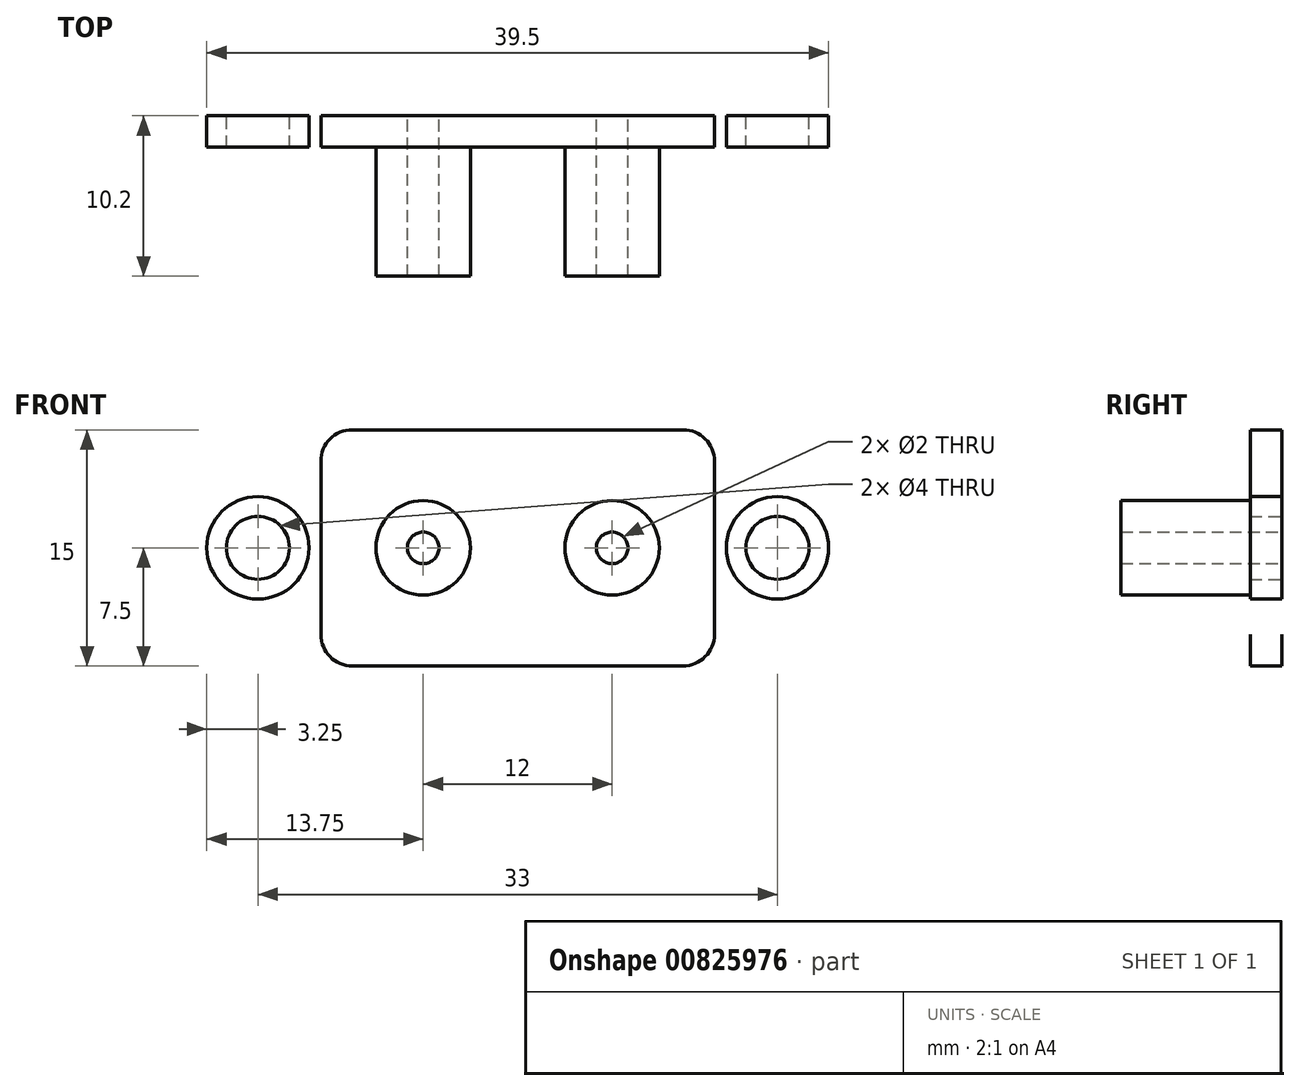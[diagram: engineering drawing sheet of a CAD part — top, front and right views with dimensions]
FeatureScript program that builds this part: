
annotation { "Feature Type Name" : "Feature", "Feature Type Description" : "" }
export const myFeature = defineFeature(function(context is Context, id is Id, definition is map)
    precondition{}
    {
        {
            var Q0;
            Q0=qCreatedBy(makeId("Front.planeOp"),FACE);
            var sketch = newSketch(context, id + "F0", { "sketchPlane" : qUnion([Q0])});
            skPoint(sketch, "E0.middle", {"position": v(0, 0) * mm});
            skLineSegment(sketch, "E1.bottom", {"start": v(10.5, -7.5) * mm, "end": v(-10.5, -7.5) * mm});
            skLineSegment(sketch, "E1.top", {"start": v(10.5, 7.5) * mm, "end": v(-10.5, 7.5) * mm});
            skLineSegment(sketch, "E1.left", {"start": v(12.5, -5.5) * mm, "end": v(12.5, 5.5) * mm});
            skLineSegment(sketch, "E1.right", {"start": v(-12.5, -5.5) * mm, "end": v(-12.5, 5.5) * mm});
            skPoint(sketch, "E2.visualSharp", {"position": v(-12.5, -7.5) * mm});
            skArc(sketch, "E2.filletArc", {"start": v(-12.5, -5.5) * mm, "mid": v(-11.91, -6.91) * mm, "end": v(-10.5, -7.5) * mm});
            skPoint(sketch, "E3.visualSharp", {"position": v(-12.5, 7.5) * mm});
            skArc(sketch, "E3.filletArc", {"start": v(-10.5, 7.5) * mm, "mid": v(-11.91, 6.91) * mm, "end": v(-12.5, 5.5) * mm});
            skPoint(sketch, "E4.visualSharp", {"position": v(12.5, -7.5) * mm});
            skArc(sketch, "E4.filletArc", {"start": v(10.5, -7.5) * mm, "mid": v(11.91, -6.91) * mm, "end": v(12.5, -5.5) * mm});
            skPoint(sketch, "E5.visualSharp", {"position": v(12.5, 7.5) * mm});
            skArc(sketch, "E5.filletArc", {"start": v(12.5, 5.5) * mm, "mid": v(11.91, 6.91) * mm, "end": v(10.5, 7.5) * mm});
            skCircle(sketch, "E6", {"center": v(-6, 0) * mm, "radius": 1 * mm});
            skCircle(sketch, "E7", {"center": v(6, 0) * mm, "radius": 1 * mm});
            skLineSegment(sketch, "E8.bottom", {"start": v(-12.5, 2) * mm, "end": v(-14.2, 2) * mm});
            skLineSegment(sketch, "E8.top", {"start": v(-12.5, -2) * mm, "end": v(-14.2, -2) * mm});
            skLineSegment(sketch, "E8.left", {"start": v(-12.5, 2) * mm, "end": v(-12.5, -2) * mm});
            skLineSegment(sketch, "E8.right", {"start": v(-14.2, 2) * mm, "end": v(-14.2, -2) * mm});
            skPoint(sketch, "E8.middle", {"position": v(-13.35, 0) * mm});
            skPoint(sketch, "E8.middle.positionSnap0", {"position": v(-12.5, 0) * mm});
            skPoint(sketch, "E8.centerSnap0", {"position": v(-12.5, 0) * mm});
            skLineSegment(sketch, "E9.bottom", {"start": v(12.5, 2) * mm, "end": v(14.2, 2) * mm});
            skLineSegment(sketch, "E9.top", {"start": v(12.5, -2) * mm, "end": v(14.2, -2) * mm});
            skLineSegment(sketch, "E9.left", {"start": v(12.5, 2) * mm, "end": v(12.5, -2) * mm});
            skLineSegment(sketch, "E9.right", {"start": v(14.2, 2) * mm, "end": v(14.2, -2) * mm});
            skPoint(sketch, "E9.middle", {"position": v(13.35, 0) * mm});
            skCircle(sketch, "E10", {"center": v(-16.5, 0) * mm, "radius": 3.25 * mm});
            skCircle(sketch, "E11", {"center": v(-16.5, 0) * mm, "radius": 2 * mm});
            skCircle(sketch, "E12", {"center": v(16.5, 0) * mm, "radius": 3.25 * mm});
            skCircle(sketch, "E13", {"center": v(16.5, 0) * mm, "radius": 2 * mm});
            skCircle(sketch, "E14", {"center": v(-6, 0) * mm, "radius": 3 * mm});
            skCircle(sketch, "E15", {"center": v(6, 0) * mm, "radius": 3 * mm});
            skSolve(sketch);
        }
        {
            var Q0;
            Q0=makeQuery(id+"F0.imprint","IMPRINT",FACE,{"disambiguationData":[TD([[makeQuery(id+"F0.imprint","IMPRINT",EDGE,{"derivedFrom":sQuery(id+"F0.wireOp",EDGE,"E1.bottom")}),-1.0]])]});
            var Q1;
            {var subQ0=sQuery(id+"F0.wireOp",EDGE,"E8.left");Q1=makeQuery(id+"F0.imprint","IMPRINT",FACE,{"disambiguationData":[TD([[makeQuery(id+"F0.imprint","IMPRINT",EDGE,{"derivedFrom":subQ0}),-1.0]])]});}
            var Q2;
            {var subQ0=sQuery(id+"F0.wireOp",EDGE,"E8.right");Q2=makeQuery(id+"F0.imprint","IMPRINT",FACE,{"disambiguationData":[TD([[makeQuery(id+"F0.imprint","IMPRINT",EDGE,{"derivedFrom":subQ0}),1.0]])]});}
            var Q3;
            {var subQ5=sQuery(id+"F0.wireOp",EDGE,"E8.right");Q3=makeQuery(id+"F0.imprint","IMPRINT",FACE,{"disambiguationData":[TD([[makeQuery(id+"F0.imprint","IMPRINT",EDGE,{"derivedFrom":subQ5}),-1.0]])]});}
            var Q4;
            {var subQ0=sQuery(id+"F0.wireOp",EDGE,"E9.left");Q4=makeQuery(id+"F0.imprint","IMPRINT",FACE,{"disambiguationData":[TD([[makeQuery(id+"F0.imprint","IMPRINT",EDGE,{"derivedFrom":subQ0}),1.0]])]});}
            var Q5;
            {var subQ0=sQuery(id+"F0.wireOp",EDGE,"E9.right");Q5=makeQuery(id+"F0.imprint","IMPRINT",FACE,{"disambiguationData":[TD([[makeQuery(id+"F0.imprint","IMPRINT",EDGE,{"derivedFrom":subQ0}),-1.0]])]});}
            var Q6;
            {var subQ5=sQuery(id+"F0.wireOp",EDGE,"E9.right");Q6=makeQuery(id+"F0.imprint","IMPRINT",FACE,{"disambiguationData":[TD([[makeQuery(id+"F0.imprint","IMPRINT",EDGE,{"derivedFrom":subQ5}),1.0]])]});}
            extrude(context, id + "F1", {"entities" : qUnion([Q0, Q1, Q2, Q3, Q4, Q5, Q6]), "depth" : 2 * mm, "offsetDistance" : 25 * mm});
        }
        {
            var Q0;
            Q0=makeQuery(id+"F0.imprint","IMPRINT",FACE,{"disambiguationData":[TD([[makeQuery(id+"F0.imprint","IMPRINT",EDGE,{"derivedFrom":sQuery(id+"F0.wireOp",EDGE,"E6")}),-1.0]])]});
            var Q1;
            Q1=makeQuery(id+"F0.imprint","IMPRINT",FACE,{"disambiguationData":[TD([[makeQuery(id+"F0.imprint","IMPRINT",EDGE,{"derivedFrom":sQuery(id+"F0.wireOp",EDGE,"E7")}),-1.0]])]});
            extrude(context, id + "F2", {"entities" : qUnion([Q0, Q1]), "operationType" : NewBodyOperationType.ADD, "depth" : 10.2 * mm, "offsetDistance" : 25 * mm});
        }
    });
